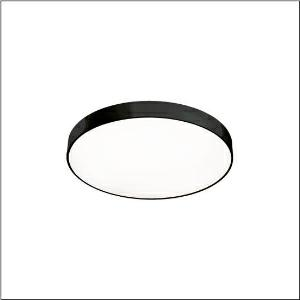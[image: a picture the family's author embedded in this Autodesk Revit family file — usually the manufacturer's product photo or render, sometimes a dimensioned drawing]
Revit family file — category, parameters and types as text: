
# Revit family: round_21_m_51mr36fd0421b
name_source: partatom
category: Lighting Fixtures
units: mm (PartAtom-declared; Revit-internal decimal feet)

## family parameters
Cut with Voids When Loaded = No
Host = Face
Light Source = No
Part Type = Normal
Room Calculation Point = No
Round Connector Dimension = Use Diameter
Shared = No

## types (1)
- Round 21 M (1 x LED, 7110 lm, 54.8 W, 4000K)
    Apparent Load = 55 VA
    CIE Flux Codes = 49 80 96 100 100
    Color Rendering = 80
    Color Temperature = 4000K
    Default Elevation = 1800 mm
    Description = Round 21 M, wall and ceiling luminaire, primary optical cover: cover, of PMMA, opal, light emission: direct distribution, primary light characteristic: symmetric, installation type: surface-mounted, suspended mounting, LED, rated luminous flux: 7.110lm, luminous efficacy: 130lm/W, light colour: 840, colour temperature: 4000K, with terminal, 5-pole, mains connection: 230V, AC, 50/60Hz, rated input power: 55W, housing, of aluminium, coated, black, diameter: 600mm, height: 62mm, protection rating (complete): IP40, insulation class (complete): insulation class I (protective earthing), certification: CE, impact resistance: IK04, permissible operating ambient temperature: -10..+35°C, packaging unit: 1 piece
    Height = 87 mm
    Lamp = 1 x LED
    Lamp Light Flux = 7110 lm
    Lamp Power = 54.8 W
    Lamp count = 1
    Length = 600 mm
    Luminous efficacy = 130 lm/W
    Manufacturer = Siteco
    ModVariant = No
    Model = 51MR36FD0421B
    Mounting Place = Ceiling
    Mounting Type = Surface mounted
    Number of Poles = 1
    OnlyDefault = Yes
    Power Factor = 1
    Product Name = Round 21 M
    Product group = wall and ceiling luminaire
    ProductGroupID = 302
    Protection Class = Protection class I
    Protection Degree = IP 40
    RLX_Detail_Level = 1
    RLX_Emergency_Light_Flux = 0 lm
    RLX_Emergency_Type = 0
    RLX_Emergency_Type_DB = No
    RlxData = <blob elided: 17705 chars, md5=006fc328>
    Socket = socket
    Standby Power = 0 W
    System Light Flux = 7110 lm
    System Power = 55 W
    Type Comments = Product without accessories
    Type Image = l_1258332.jpg
    URL = http://relux.com
    VarID = ---
    Voltage = 0 V
    Weight = 0.00 kg
    Width = 0 mm  [stored 0 ft]

note: [stored X ft] marks values corroborated as IEEE doubles in the binary element streams (Revit-internal decimal feet)

## geometry (parser evidence)
native form markers: Blend x4, Sweep x11
no freeform markers — native parametric forms only
